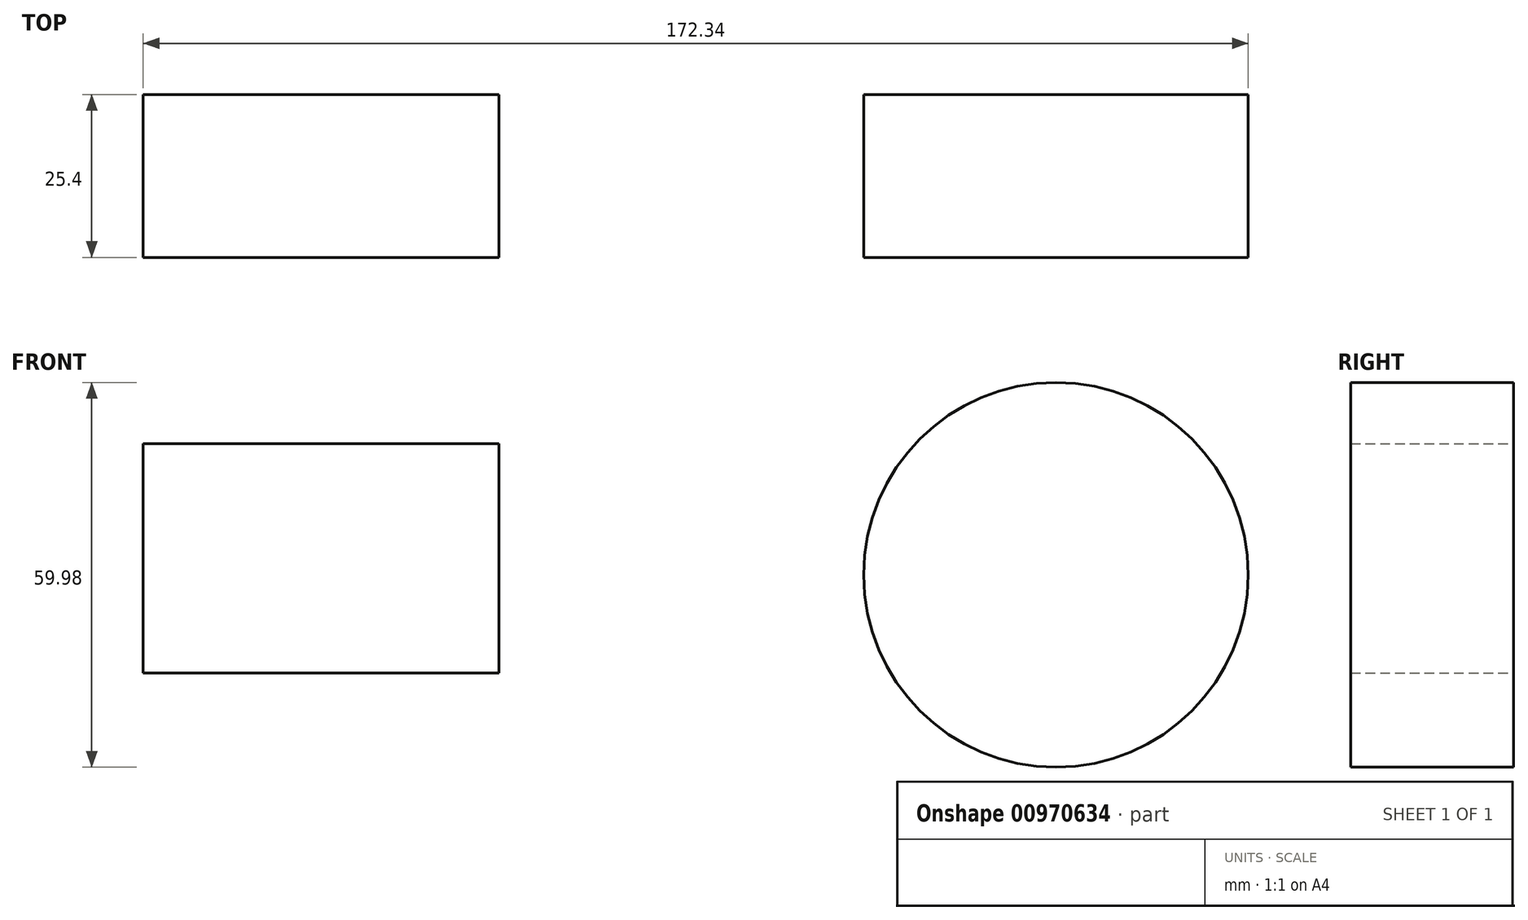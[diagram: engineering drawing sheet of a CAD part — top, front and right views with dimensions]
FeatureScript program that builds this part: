
annotation { "Feature Type Name" : "Feature", "Feature Type Description" : "" }
export const myFeature = defineFeature(function(context is Context, id is Id, definition is map)
    precondition{}
    {
        {
            var Q0;
            Q0=qCreatedBy(makeId("Front.planeOp"),FACE);
            var sketch = newSketch(context, id + "F0", { "sketchPlane" : qUnion([Q0])});
            skLineSegment(sketch, "E0.bottom", {"start": v(-84.59, 53.92) * mm, "end": v(-29.11, 53.92) * mm});
            skLineSegment(sketch, "E0.top", {"start": v(-84.59, 18.12) * mm, "end": v(-29.11, 18.12) * mm});
            skLineSegment(sketch, "E0.left", {"start": v(-84.59, 53.92) * mm, "end": v(-84.59, 18.12) * mm});
            skLineSegment(sketch, "E0.right", {"start": v(-29.11, 53.92) * mm, "end": v(-29.11, 18.12) * mm});
            skCircle(sketch, "E1", {"center": v(57.76, 33.44) * mm, "radius": 29.99 * mm});
            skSolve(sketch);
        }
        {
            var Q0;
            Q0 = qSketchRegion(id + "F0", true);
            extrude(context, id + "F1", {"entities" : qUnion([Q0]), "depth" : 25.4 * mm, "offsetDistance" : 25.4 * mm});
        }
    });
